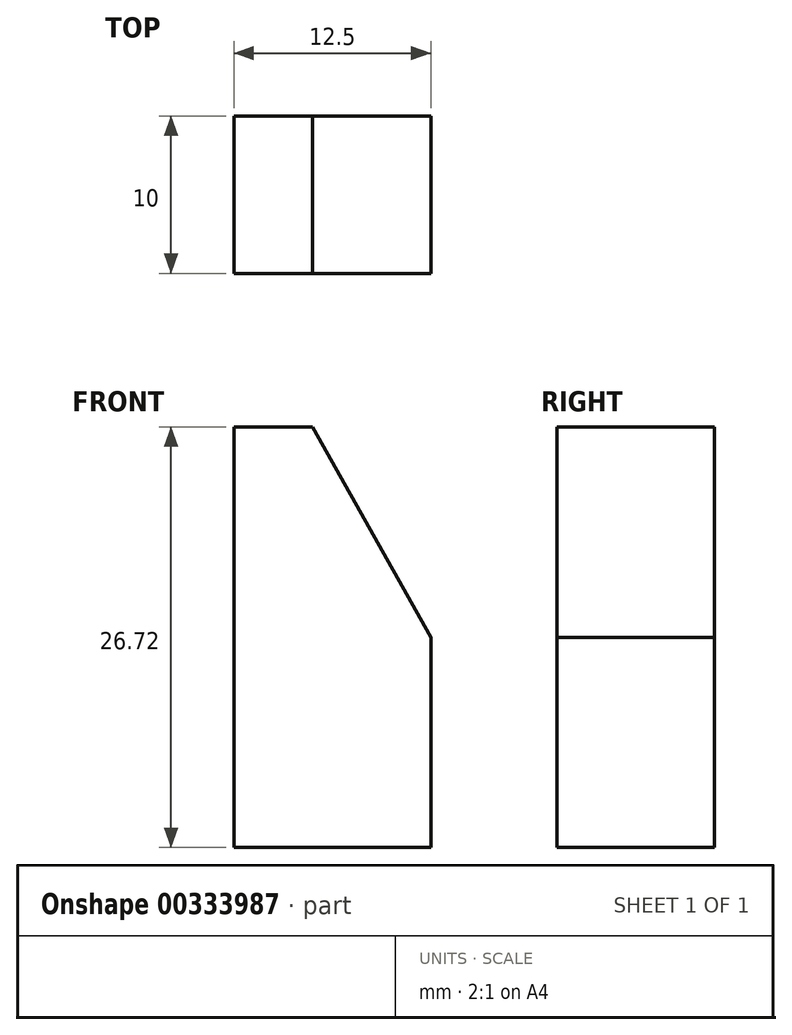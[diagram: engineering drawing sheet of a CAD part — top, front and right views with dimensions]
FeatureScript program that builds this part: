
annotation { "Feature Type Name" : "Feature", "Feature Type Description" : "" }
export const myFeature = defineFeature(function(context is Context, id is Id, definition is map)
    precondition{}
    {
        {
            var Q0;
            Q0=qCreatedBy(makeId("Front.planeOp"),FACE);
            var sketch = newSketch(context, id + "F0", { "sketchPlane" : qUnion([Q0])});
            skLineSegment(sketch, "E0.bottom", {"start": v(-1.25, 13.36) * mm, "end": v(-6.25, 13.36) * mm});
            skLineSegment(sketch, "E0.top", {"start": v(6.25, -13.36) * mm, "end": v(-6.25, -13.36) * mm});
            skLineSegment(sketch, "E0.left", {"start": v(6.25, 0) * mm, "end": v(6.25, -13.36) * mm});
            skLineSegment(sketch, "E0.right", {"start": v(-6.25, 13.36) * mm, "end": v(-6.25, -13.36) * mm});
            skPoint(sketch, "E0.middle", {"position": v(0, 0) * mm});
            skLineSegment(sketch, "E1", {"start": v(-1.25, 13.36) * mm, "end": v(6.25, 0) * mm});
            skSolve(sketch);
        }
        {
            var Q0;
            Q0=makeQuery(id+"F0.imprint","IMPRINT",FACE,{"disambiguationData":[TD([[makeQuery(id+"F0.imprint","IMPRINT",EDGE,{"derivedFrom":sQuery(id+"F0.wireOp",EDGE,"E0.bottom")}),1.0]])]});
            extrude(context, id + "F1", {"entities" : qUnion([Q0]), "depth" : 10 * mm});
        }
    });
